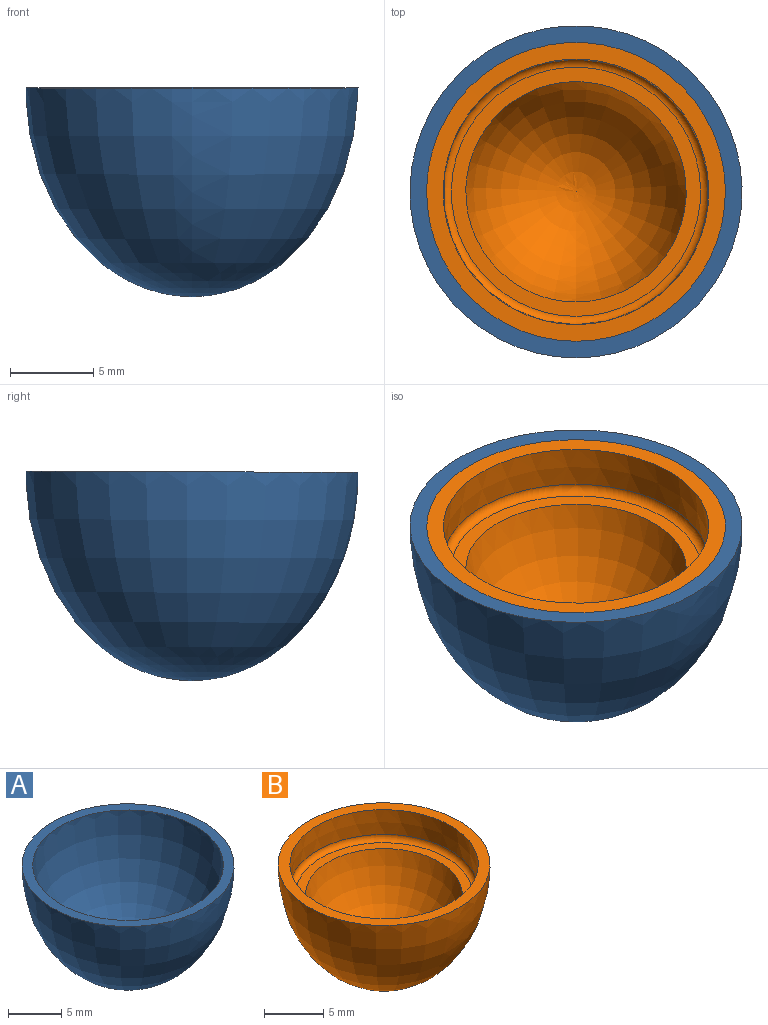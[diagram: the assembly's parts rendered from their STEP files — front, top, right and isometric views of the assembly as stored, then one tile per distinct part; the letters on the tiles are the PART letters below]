
ASSEMBLY  parts=2 mates=1
PART A: 3 faces, bbox 19.9x19.9x12.6 mm
  f0: revolved ~17.93x17.93mm, area 606.5mm2, adj f1
  f1: cone r=8.97mm half-angle=89.7deg, axis (0,0,1), area 59.5mm2, adj f0,f2
  f2: revolved ~19.93x19.93mm, area 737.3mm2, adj f1
PART B: 6 faces, bbox 17.9x17.9x11.5 mm
  f0: revolved ~17.93x17.93mm, area 606.5mm2, adj f5
  f1: revolved ~13.22x13.22mm, area 249.2mm2, adj f2
  f2: cone r=7.47mm half-angle=89.8deg, axis (0,0,1), area 38.1mm2, adj f1,f3
  f3: torus R=7.47mm, axis (0,0,1), area 38.4mm2, adj f2,f4
  f4: cone r=7.97mm half-angle=0.2deg, axis (0,0,-1), area 128.9mm2, adj f3,f5
  f5: cone r=8.97mm half-angle=89.7deg, axis (0,0,1), area 53.2mm2, adj f0,f4
PLACE A t=(-4.64,-7.71,-1.32)mm
PLACE B t=(-4.64,-7.71,-1.32)mm
MATE fastened B.f4 <-> A.f1  axis (0,0,1) through (-4.64,-7.72,-9.58)mm
